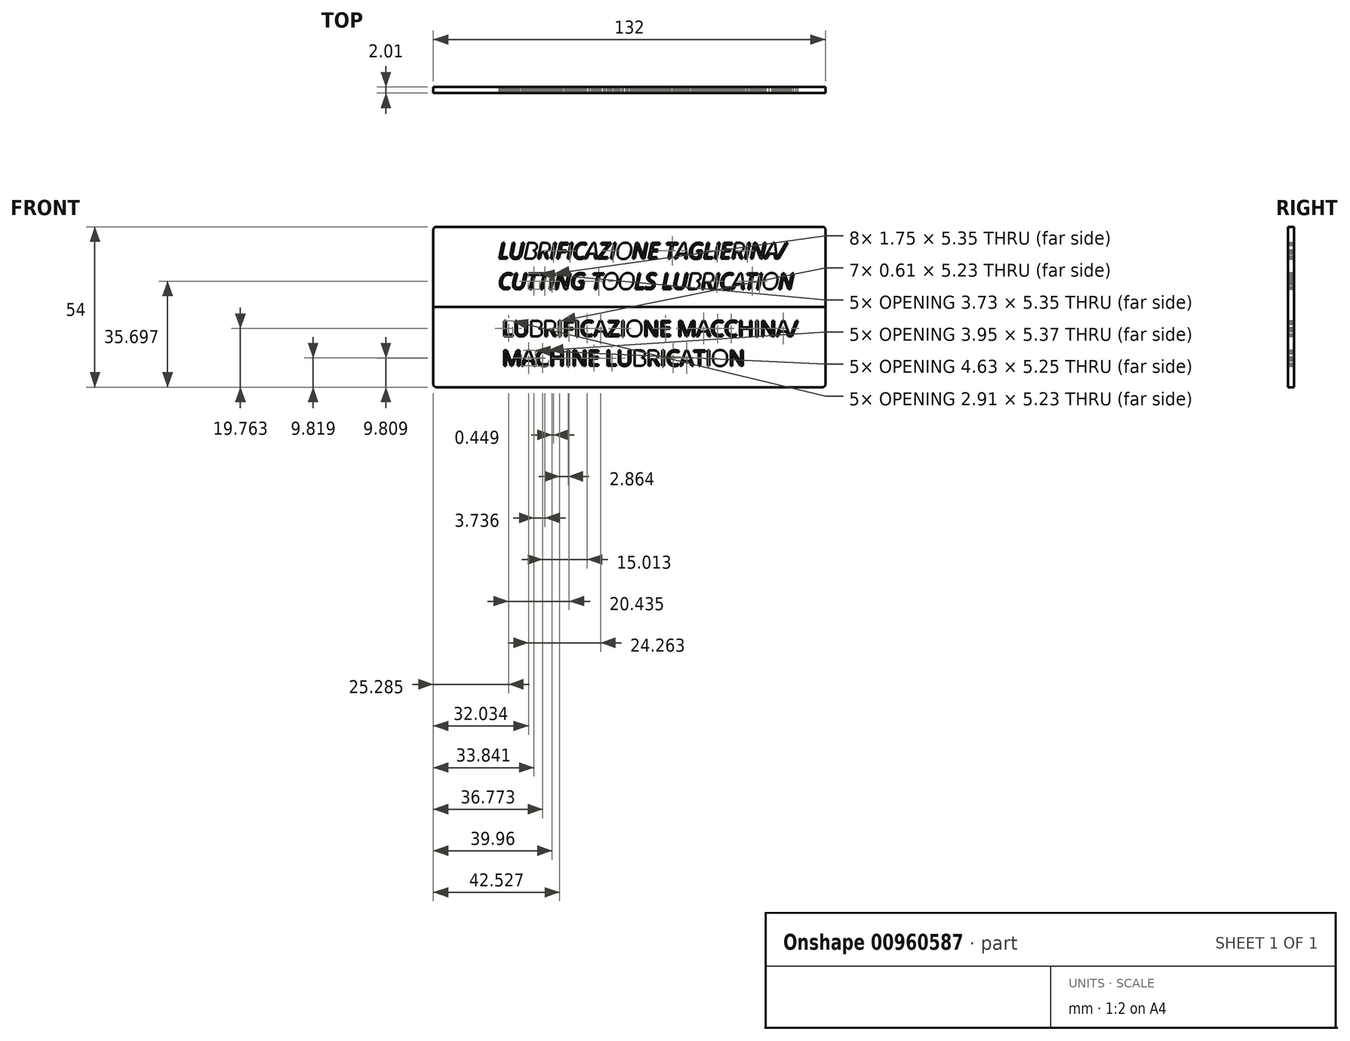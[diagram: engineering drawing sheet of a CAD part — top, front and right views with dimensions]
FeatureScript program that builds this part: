
annotation { "Feature Type Name" : "Feature", "Feature Type Description" : "" }
export const myFeature = defineFeature(function(context is Context, id is Id, definition is map)
    precondition{}
    {
        {
            var Q0;
            Q0=qCreatedBy(makeId("Front.planeOp"),FACE);
            var sketch = newSketch(context, id + "F0", { "sketchPlane" : qUnion([Q0])});
            skLineSegment(sketch, "E0.bottom", {"start": v(65, -27) * mm, "end": v(-65, -27) * mm});
            skLineSegment(sketch, "E0.top", {"start": v(65, 27) * mm, "end": v(-65, 27) * mm});
            skLineSegment(sketch, "E0.left", {"start": v(66, -26) * mm, "end": v(66, 26) * mm});
            skLineSegment(sketch, "E0.right", {"start": v(-66, -26) * mm, "end": v(-66, 26) * mm});
            skPoint(sketch, "E0.middle", {"position": v(0, 0) * mm});
            skLineSegment(sketch, "E1", {"start": v(-66, 0) * mm, "end": v(66, 0) * mm});
            skPoint(sketch, "E2.visualSharp", {"position": v(-66, 27) * mm});
            skArc(sketch, "E2.filletArc", {"start": v(-65, 27) * mm, "mid": v(-65.7, 26.7) * mm, "end": v(-66, 26) * mm});
            skPoint(sketch, "E3.visualSharp", {"position": v(66, 27) * mm});
            skArc(sketch, "E3.filletArc", {"start": v(66, 26) * mm, "mid": v(65.7, 26.7) * mm, "end": v(65, 27) * mm});
            skPoint(sketch, "E4.visualSharp", {"position": v(66, -27) * mm});
            skArc(sketch, "E4.filletArc", {"start": v(65, -27) * mm, "mid": v(65.7, -26.7) * mm, "end": v(66, -26) * mm});
            skPoint(sketch, "E5.visualSharp", {"position": v(-66, -27) * mm});
            skArc(sketch, "E5.filletArc", {"start": v(-66, -26) * mm, "mid": v(-65.7, -26.7) * mm, "end": v(-65, -27) * mm});
            skText(sketch, "E6", { "text": "LUBRIFICAZIONE TAGLIERINA/\nCUTTING TOOLS LUBRICATION", "fontName": "OpenSans-Italic.ttf"});
            skText(sketch, "E7", { "text": "LUBRIFICAZIONE MACCHINA/ \nMACHINE LUBRICATION", "fontName": "OpenSans-Regular.ttf"});
            const initialGuessF0  = {"E6": [-0.04416, 0.01622, 1, 0, 0.0054], "E7": [-0.04289, -0.00985, 1, 0, 0.00527]};
            skSetInitialGuess(sketch, initialGuessF0);
            skSolve(sketch);
        }
        {
            var Q0;
            Q0 = qSketchRegion(id + "F0", true);
            extrude(context, id + "F1", {"entities" : qUnion([Q0]), "depth" : 2 * mm, "offsetDistance" : 25 * mm});
        }
        {
            var Q0;
            Q0=makeQuery(id+"F1.opExtrude","CAP_FACE",FACE,{"disambiguationData":[OSD([sQuery(id+"F0.wireOp",EDGE,"E0.bottom"),sQuery(id+"F0.wireOp",EDGE,"E0.top"),sQuery(id+"F0.wireOp",EDGE,"E0.left"),sQuery(id+"F0.wireOp",EDGE,"E0.right"),sQuery(id+"F0.wireOp",EDGE,"E2.filletArc"),sQuery(id+"F0.wireOp",EDGE,"E3.filletArc"),sQuery(id+"F0.wireOp",EDGE,"E4.filletArc"),sQuery(id+"F0.wireOp",EDGE,"E5.filletArc"),sQuery(id+"F0.wireOp",EDGE,"E6.sketch_text.stroke-0"),sQuery(id+"F0.wireOp",EDGE,"E6.sketch_text.stroke-1"),sQuery(id+"F0.wireOp",EDGE,"E6.sketch_text.stroke-2"),sQuery(id+"F0.wireOp",EDGE,"E6.sketch_text.stroke-3"),sQuery(id+"F0.wireOp",EDGE,"E6.sketch_text.stroke-4"),sQuery(id+"F0.wireOp",EDGE,"E6.sketch_text.stroke-5"),sQuery(id+"F0.wireOp",EDGE,"E6.sketch_text.stroke-6"),sQuery(id+"F0.wireOp",EDGE,"E6.sketch_text.stroke-7"),sQuery(id+"F0.wireOp",EDGE,"E6.sketch_text.stroke-8"),sQuery(id+"F0.wireOp",EDGE,"E6.sketch_text.stroke-9"),sQuery(id+"F0.wireOp",EDGE,"E6.sketch_text.stroke-10"),sQuery(id+"F0.wireOp",EDGE,"E6.sketch_text.stroke-11"),sQuery(id+"F0.wireOp",EDGE,"E6.sketch_text.stroke-12"),sQuery(id+"F0.wireOp",EDGE,"E6.sketch_text.stroke-13"),sQuery(id+"F0.wireOp",EDGE,"E6.sketch_text.stroke-14"),sQuery(id+"F0.wireOp",EDGE,"E6.sketch_text.stroke-15"),sQuery(id+"F0.wireOp",EDGE,"E6.sketch_text.stroke-16"),sQuery(id+"F0.wireOp",EDGE,"E6.sketch_text.stroke-17"),sQuery(id+"F0.wireOp",EDGE,"E6.sketch_text.stroke-18"),sQuery(id+"F0.wireOp",EDGE,"E6.sketch_text.stroke-19"),sQuery(id+"F0.wireOp",EDGE,"E6.sketch_text.stroke-20"),sQuery(id+"F0.wireOp",EDGE,"E6.sketch_text.stroke-21"),sQuery(id+"F0.wireOp",EDGE,"E6.sketch_text.stroke-22"),sQuery(id+"F0.wireOp",EDGE,"E6.sketch_text.stroke-23"),sQuery(id+"F0.wireOp",EDGE,"E6.sketch_text.stroke-24"),sQuery(id+"F0.wireOp",EDGE,"E6.sketch_text.stroke-25"),sQuery(id+"F0.wireOp",EDGE,"E6.sketch_text.stroke-26"),sQuery(id+"F0.wireOp",EDGE,"E6.sketch_text.stroke-27"),sQuery(id+"F0.wireOp",EDGE,"E6.sketch_text.stroke-28"),sQuery(id+"F0.wireOp",EDGE,"E6.sketch_text.stroke-29"),sQuery(id+"F0.wireOp",EDGE,"E6.sketch_text.stroke-30"),sQuery(id+"F0.wireOp",EDGE,"E6.sketch_text.stroke-31"),sQuery(id+"F0.wireOp",EDGE,"E6.sketch_text.stroke-32"),sQuery(id+"F0.wireOp",EDGE,"E6.sketch_text.stroke-47"),sQuery(id+"F0.wireOp",EDGE,"E6.sketch_text.stroke-48"),sQuery(id+"F0.wireOp",EDGE,"E6.sketch_text.stroke-49"),sQuery(id+"F0.wireOp",EDGE,"E6.sketch_text.stroke-50"),sQuery(id+"F0.wireOp",EDGE,"E6.sketch_text.stroke-51"),sQuery(id+"F0.wireOp",EDGE,"E6.sketch_text.stroke-52"),sQuery(id+"F0.wireOp",EDGE,"E6.sketch_text.stroke-53"),sQuery(id+"F0.wireOp",EDGE,"E6.sketch_text.stroke-54"),sQuery(id+"F0.wireOp",EDGE,"E6.sketch_text.stroke-55"),sQuery(id+"F0.wireOp",EDGE,"E6.sketch_text.stroke-56"),sQuery(id+"F0.wireOp",EDGE,"E6.sketch_text.stroke-64"),sQuery(id+"F0.wireOp",EDGE,"E6.sketch_text.stroke-65"),sQuery(id+"F0.wireOp",EDGE,"E6.sketch_text.stroke-66"),sQuery(id+"F0.wireOp",EDGE,"E6.sketch_text.stroke-67"),sQuery(id+"F0.wireOp",EDGE,"E6.sketch_text.stroke-68"),sQuery(id+"F0.wireOp",EDGE,"E6.sketch_text.stroke-69"),sQuery(id+"F0.wireOp",EDGE,"E6.sketch_text.stroke-70"),sQuery(id+"F0.wireOp",EDGE,"E6.sketch_text.stroke-71"),sQuery(id+"F0.wireOp",EDGE,"E6.sketch_text.stroke-72"),sQuery(id+"F0.wireOp",EDGE,"E6.sketch_text.stroke-73"),sQuery(id+"F0.wireOp",EDGE,"E6.sketch_text.stroke-74"),sQuery(id+"F0.wireOp",EDGE,"E6.sketch_text.stroke-75"),sQuery(id+"F0.wireOp",EDGE,"E6.sketch_text.stroke-76"),sQuery(id+"F0.wireOp",EDGE,"E6.sketch_text.stroke-77"),sQuery(id+"F0.wireOp",EDGE,"E6.sketch_text.stroke-78"),sQuery(id+"F0.wireOp",EDGE,"E6.sketch_text.stroke-79"),sQuery(id+"F0.wireOp",EDGE,"E6.sketch_text.stroke-80"),sQuery(id+"F0.wireOp",EDGE,"E6.sketch_text.stroke-81"),sQuery(id+"F0.wireOp",EDGE,"E6.sketch_text.stroke-82"),sQuery(id+"F0.wireOp",EDGE,"E6.sketch_text.stroke-83"),sQuery(id+"F0.wireOp",EDGE,"E6.sketch_text.stroke-84"),sQuery(id+"F0.wireOp",EDGE,"E6.sketch_text.stroke-85"),sQuery(id+"F0.wireOp",EDGE,"E6.sketch_text.stroke-86"),sQuery(id+"F0.wireOp",EDGE,"E6.sketch_text.stroke-87"),sQuery(id+"F0.wireOp",EDGE,"E6.sketch_text.stroke-88"),sQuery(id+"F0.wireOp",EDGE,"E6.sketch_text.stroke-89"),sQuery(id+"F0.wireOp",EDGE,"E6.sketch_text.stroke-90"),sQuery(id+"F0.wireOp",EDGE,"E6.sketch_text.stroke-91"),sQuery(id+"F0.wireOp",EDGE,"E6.sketch_text.stroke-92"),sQuery(id+"F0.wireOp",EDGE,"E6.sketch_text.stroke-93"),sQuery(id+"F0.wireOp",EDGE,"E6.sketch_text.stroke-94"),sQuery(id+"F0.wireOp",EDGE,"E6.sketch_text.stroke-95"),sQuery(id+"F0.wireOp",EDGE,"E6.sketch_text.stroke-96"),sQuery(id+"F0.wireOp",EDGE,"E6.sketch_text.stroke-97"),sQuery(id+"F0.wireOp",EDGE,"E6.sketch_text.stroke-98"),sQuery(id+"F0.wireOp",EDGE,"E6.sketch_text.stroke-99"),sQuery(id+"F0.wireOp",EDGE,"E6.sketch_text.stroke-100"),sQuery(id+"F0.wireOp",EDGE,"E6.sketch_text.stroke-101"),sQuery(id+"F0.wireOp",EDGE,"E6.sketch_text.stroke-102"),sQuery(id+"F0.wireOp",EDGE,"E6.sketch_text.stroke-103"),sQuery(id+"F0.wireOp",EDGE,"E6.sketch_text.stroke-104"),sQuery(id+"F0.wireOp",EDGE,"E6.sketch_text.stroke-105"),sQuery(id+"F0.wireOp",EDGE,"E6.sketch_text.stroke-106"),sQuery(id+"F0.wireOp",EDGE,"E6.sketch_text.stroke-112"),sQuery(id+"F0.wireOp",EDGE,"E6.sketch_text.stroke-113"),sQuery(id+"F0.wireOp",EDGE,"E6.sketch_text.stroke-114"),sQuery(id+"F0.wireOp",EDGE,"E6.sketch_text.stroke-115"),sQuery(id+"F0.wireOp",EDGE,"E6.sketch_text.stroke-116"),sQuery(id+"F0.wireOp",EDGE,"E6.sketch_text.stroke-117"),sQuery(id+"F0.wireOp",EDGE,"E6.sketch_text.stroke-118"),sQuery(id+"F0.wireOp",EDGE,"E6.sketch_text.stroke-119"),sQuery(id+"F0.wireOp",EDGE,"E6.sketch_text.stroke-120"),sQuery(id+"F0.wireOp",EDGE,"E6.sketch_text.stroke-121"),sQuery(id+"F0.wireOp",EDGE,"E6.sketch_text.stroke-122"),sQuery(id+"F0.wireOp",EDGE,"E6.sketch_text.stroke-123"),sQuery(id+"F0.wireOp",EDGE,"E6.sketch_text.stroke-124"),sQuery(id+"F0.wireOp",EDGE,"E6.sketch_text.stroke-125"),sQuery(id+"F0.wireOp",EDGE,"E6.sketch_text.stroke-126"),sQuery(id+"F0.wireOp",EDGE,"E6.sketch_text.stroke-127"),sQuery(id+"F0.wireOp",EDGE,"E6.sketch_text.stroke-128"),sQuery(id+"F0.wireOp",EDGE,"E6.sketch_text.stroke-129"),sQuery(id+"F0.wireOp",EDGE,"E6.sketch_text.stroke-130"),sQuery(id+"F0.wireOp",EDGE,"E6.sketch_text.stroke-131"),sQuery(id+"F0.wireOp",EDGE,"E6.sketch_text.stroke-132"),sQuery(id+"F0.wireOp",EDGE,"E6.sketch_text.stroke-133"),sQuery(id+"F0.wireOp",EDGE,"E6.sketch_text.stroke-134"),sQuery(id+"F0.wireOp",EDGE,"E6.sketch_text.stroke-135"),sQuery(id+"F0.wireOp",EDGE,"E6.sketch_text.stroke-146"),sQuery(id+"F0.wireOp",EDGE,"E6.sketch_text.stroke-147"),sQuery(id+"F0.wireOp",EDGE,"E6.sketch_text.stroke-148"),sQuery(id+"F0.wireOp",EDGE,"E6.sketch_text.stroke-149"),sQuery(id+"F0.wireOp",EDGE,"E6.sketch_text.stroke-150"),sQuery(id+"F0.wireOp",EDGE,"E6.sketch_text.stroke-151"),sQuery(id+"F0.wireOp",EDGE,"E6.sketch_text.stroke-152"),sQuery(id+"F0.wireOp",EDGE,"E6.sketch_text.stroke-153"),sQuery(id+"F0.wireOp",EDGE,"E6.sketch_text.stroke-154"),sQuery(id+"F0.wireOp",EDGE,"E6.sketch_text.stroke-155"),sQuery(id+"F0.wireOp",EDGE,"E6.sketch_text.stroke-156"),sQuery(id+"F0.wireOp",EDGE,"E6.sketch_text.stroke-157"),sQuery(id+"F0.wireOp",EDGE,"E6.sketch_text.stroke-158"),sQuery(id+"F0.wireOp",EDGE,"E6.sketch_text.stroke-159"),sQuery(id+"F0.wireOp",EDGE,"E6.sketch_text.stroke-160"),sQuery(id+"F0.wireOp",EDGE,"E6.sketch_text.stroke-161"),sQuery(id+"F0.wireOp",EDGE,"E6.sketch_text.stroke-162"),sQuery(id+"F0.wireOp",EDGE,"E6.sketch_text.stroke-163"),sQuery(id+"F0.wireOp",EDGE,"E6.sketch_text.stroke-164"),sQuery(id+"F0.wireOp",EDGE,"E6.sketch_text.stroke-165"),sQuery(id+"F0.wireOp",EDGE,"E6.sketch_text.stroke-166"),sQuery(id+"F0.wireOp",EDGE,"E6.sketch_text.stroke-167"),sQuery(id+"F0.wireOp",EDGE,"E6.sketch_text.stroke-168"),sQuery(id+"F0.wireOp",EDGE,"E6.sketch_text.stroke-169"),sQuery(id+"F0.wireOp",EDGE,"E6.sketch_text.stroke-170"),sQuery(id+"F0.wireOp",EDGE,"E6.sketch_text.stroke-171"),sQuery(id+"F0.wireOp",EDGE,"E6.sketch_text.stroke-172"),sQuery(id+"F0.wireOp",EDGE,"E6.sketch_text.stroke-173"),sQuery(id+"F0.wireOp",EDGE,"E6.sketch_text.stroke-174"),sQuery(id+"F0.wireOp",EDGE,"E6.sketch_text.stroke-175"),sQuery(id+"F0.wireOp",EDGE,"E6.sketch_text.stroke-176"),sQuery(id+"F0.wireOp",EDGE,"E6.sketch_text.stroke-177"),sQuery(id+"F0.wireOp",EDGE,"E6.sketch_text.stroke-178"),sQuery(id+"F0.wireOp",EDGE,"E6.sketch_text.stroke-179"),sQuery(id+"F0.wireOp",EDGE,"E6.sketch_text.stroke-180"),sQuery(id+"F0.wireOp",EDGE,"E6.sketch_text.stroke-181"),sQuery(id+"F0.wireOp",EDGE,"E6.sketch_text.stroke-182"),sQuery(id+"F0.wireOp",EDGE,"E6.sketch_text.stroke-183"),sQuery(id+"F0.wireOp",EDGE,"E6.sketch_text.stroke-184"),sQuery(id+"F0.wireOp",EDGE,"E6.sketch_text.stroke-185"),sQuery(id+"F0.wireOp",EDGE,"E6.sketch_text.stroke-186"),sQuery(id+"F0.wireOp",EDGE,"E6.sketch_text.stroke-187"),sQuery(id+"F0.wireOp",EDGE,"E6.sketch_text.stroke-193"),sQuery(id+"F0.wireOp",EDGE,"E6.sketch_text.stroke-194"),sQuery(id+"F0.wireOp",EDGE,"E6.sketch_text.stroke-195"),sQuery(id+"F0.wireOp",EDGE,"E6.sketch_text.stroke-196"),sQuery(id+"F0.wireOp",EDGE,"E6.sketch_text.stroke-197"),sQuery(id+"F0.wireOp",EDGE,"E6.sketch_text.stroke-198"),sQuery(id+"F0.wireOp",EDGE,"E6.sketch_text.stroke-199"),sQuery(id+"F0.wireOp",EDGE,"E6.sketch_text.stroke-200"),sQuery(id+"F0.wireOp",EDGE,"E6.sketch_text.stroke-201"),sQuery(id+"F0.wireOp",EDGE,"E6.sketch_text.stroke-202"),sQuery(id+"F0.wireOp",EDGE,"E6.sketch_text.stroke-203"),sQuery(id+"F0.wireOp",EDGE,"E6.sketch_text.stroke-204"),sQuery(id+"F0.wireOp",EDGE,"E6.sketch_text.stroke-205"),sQuery(id+"F0.wireOp",EDGE,"E6.sketch_text.stroke-206"),sQuery(id+"F0.wireOp",EDGE,"E6.sketch_text.stroke-207"),sQuery(id+"F0.wireOp",EDGE,"E6.sketch_text.stroke-208"),sQuery(id+"F0.wireOp",EDGE,"E6.sketch_text.stroke-209"),sQuery(id+"F0.wireOp",EDGE,"E6.sketch_text.stroke-210"),sQuery(id+"F0.wireOp",EDGE,"E6.sketch_text.stroke-211"),sQuery(id+"F0.wireOp",EDGE,"E6.sketch_text.stroke-212"),sQuery(id+"F0.wireOp",EDGE,"E6.sketch_text.stroke-213"),sQuery(id+"F0.wireOp",EDGE,"E6.sketch_text.stroke-214"),sQuery(id+"F0.wireOp",EDGE,"E6.sketch_text.stroke-215"),sQuery(id+"F0.wireOp",EDGE,"E6.sketch_text.stroke-216"),sQuery(id+"F0.wireOp",EDGE,"E6.sketch_text.stroke-217"),sQuery(id+"F0.wireOp",EDGE,"E6.sketch_text.stroke-218"),sQuery(id+"F0.wireOp",EDGE,"E6.sketch_text.stroke-219"),sQuery(id+"F0.wireOp",EDGE,"E6.sketch_text.stroke-220"),sQuery(id+"F0.wireOp",EDGE,"E6.sketch_text.stroke-221"),sQuery(id+"F0.wireOp",EDGE,"E6.sketch_text.stroke-222"),sQuery(id+"F0.wireOp",EDGE,"E6.sketch_text.stroke-223"),sQuery(id+"F0.wireOp",EDGE,"E6.sketch_text.stroke-224"),sQuery(id+"F0.wireOp",EDGE,"E6.sketch_text.stroke-225"),sQuery(id+"F0.wireOp",EDGE,"E6.sketch_text.stroke-226"),sQuery(id+"F0.wireOp",EDGE,"E6.sketch_text.stroke-227"),sQuery(id+"F0.wireOp",EDGE,"E6.sketch_text.stroke-228"),sQuery(id+"F0.wireOp",EDGE,"E6.sketch_text.stroke-229"),sQuery(id+"F0.wireOp",EDGE,"E6.sketch_text.stroke-230"),sQuery(id+"F0.wireOp",EDGE,"E6.sketch_text.stroke-231"),sQuery(id+"F0.wireOp",EDGE,"E6.sketch_text.stroke-232"),sQuery(id+"F0.wireOp",EDGE,"E6.sketch_text.stroke-233"),sQuery(id+"F0.wireOp",EDGE,"E6.sketch_text.stroke-234"),sQuery(id+"F0.wireOp",EDGE,"E6.sketch_text.stroke-235"),sQuery(id+"F0.wireOp",EDGE,"E6.sketch_text.stroke-236"),sQuery(id+"F0.wireOp",EDGE,"E6.sketch_text.stroke-237"),sQuery(id+"F0.wireOp",EDGE,"E6.sketch_text.stroke-238"),sQuery(id+"F0.wireOp",EDGE,"E6.sketch_text.stroke-239"),sQuery(id+"F0.wireOp",EDGE,"E6.sketch_text.stroke-240"),sQuery(id+"F0.wireOp",EDGE,"E6.sketch_text.stroke-241"),sQuery(id+"F0.wireOp",EDGE,"E6.sketch_text.stroke-242"),sQuery(id+"F0.wireOp",EDGE,"E6.sketch_text.stroke-243"),sQuery(id+"F0.wireOp",EDGE,"E6.sketch_text.stroke-244"),sQuery(id+"F0.wireOp",EDGE,"E6.sketch_text.stroke-245"),sQuery(id+"F0.wireOp",EDGE,"E6.sketch_text.stroke-246"),sQuery(id+"F0.wireOp",EDGE,"E6.sketch_text.stroke-254"),sQuery(id+"F0.wireOp",EDGE,"E6.sketch_text.stroke-255"),sQuery(id+"F0.wireOp",EDGE,"E6.sketch_text.stroke-256"),sQuery(id+"F0.wireOp",EDGE,"E6.sketch_text.stroke-257"),sQuery(id+"F0.wireOp",EDGE,"E6.sketch_text.stroke-258"),sQuery(id+"F0.wireOp",EDGE,"E6.sketch_text.stroke-259"),sQuery(id+"F0.wireOp",EDGE,"E6.sketch_text.stroke-260"),sQuery(id+"F0.wireOp",EDGE,"E6.sketch_text.stroke-261"),sQuery(id+"F0.wireOp",EDGE,"E6.sketch_text.stroke-262"),sQuery(id+"F0.wireOp",EDGE,"E6.sketch_text.stroke-263"),sQuery(id+"F0.wireOp",EDGE,"E6.sketch_text.stroke-264"),sQuery(id+"F0.wireOp",EDGE,"E6.sketch_text.stroke-265"),sQuery(id+"F0.wireOp",EDGE,"E6.sketch_text.stroke-266"),sQuery(id+"F0.wireOp",EDGE,"E6.sketch_text.stroke-267"),sQuery(id+"F0.wireOp",EDGE,"E6.sketch_text.stroke-268"),sQuery(id+"F0.wireOp",EDGE,"E6.sketch_text.stroke-269"),sQuery(id+"F0.wireOp",EDGE,"E6.sketch_text.stroke-270"),sQuery(id+"F0.wireOp",EDGE,"E6.sketch_text.stroke-271"),sQuery(id+"F0.wireOp",EDGE,"E6.sketch_text.stroke-272"),sQuery(id+"F0.wireOp",EDGE,"E6.sketch_text.stroke-273"),sQuery(id+"F0.wireOp",EDGE,"E6.sketch_text.stroke-274"),sQuery(id+"F0.wireOp",EDGE,"E6.sketch_text.stroke-275"),sQuery(id+"F0.wireOp",EDGE,"E6.sketch_text.stroke-276"),sQuery(id+"F0.wireOp",EDGE,"E6.sketch_text.stroke-277"),sQuery(id+"F0.wireOp",EDGE,"E6.sketch_text.stroke-278"),sQuery(id+"F0.wireOp",EDGE,"E6.sketch_text.stroke-279"),sQuery(id+"F0.wireOp",EDGE,"E6.sketch_text.stroke-285"),sQuery(id+"F0.wireOp",EDGE,"E6.sketch_text.stroke-286"),sQuery(id+"F0.wireOp",EDGE,"E6.sketch_text.stroke-287"),sQuery(id+"F0.wireOp",EDGE,"E6.sketch_text.stroke-288"),sQuery(id+"F0.wireOp",EDGE,"E6.sketch_text.stroke-289"),sQuery(id+"F0.wireOp",EDGE,"E6.sketch_text.stroke-290"),sQuery(id+"F0.wireOp",EDGE,"E6.sketch_text.stroke-291"),sQuery(id+"F0.wireOp",EDGE,"E6.sketch_text.stroke-292"),sQuery(id+"F0.wireOp",EDGE,"E6.sketch_text.stroke-293"),sQuery(id+"F0.wireOp",EDGE,"E6.sketch_text.stroke-294"),sQuery(id+"F0.wireOp",EDGE,"E6.sketch_text.stroke-295"),sQuery(id+"F0.wireOp",EDGE,"E6.sketch_text.stroke-296"),sQuery(id+"F0.wireOp",EDGE,"E6.sketch_text.stroke-297"),sQuery(id+"F0.wireOp",EDGE,"E6.sketch_text.stroke-298"),sQuery(id+"F0.wireOp",EDGE,"E6.sketch_text.stroke-299"),sQuery(id+"F0.wireOp",EDGE,"E6.sketch_text.stroke-300"),sQuery(id+"F0.wireOp",EDGE,"E6.sketch_text.stroke-301"),sQuery(id+"F0.wireOp",EDGE,"E6.sketch_text.stroke-302"),sQuery(id+"F0.wireOp",EDGE,"E6.sketch_text.stroke-303"),sQuery(id+"F0.wireOp",EDGE,"E6.sketch_text.stroke-304"),sQuery(id+"F0.wireOp",EDGE,"E6.sketch_text.stroke-305"),sQuery(id+"F0.wireOp",EDGE,"E6.sketch_text.stroke-306"),sQuery(id+"F0.wireOp",EDGE,"E6.sketch_text.stroke-307"),sQuery(id+"F0.wireOp",EDGE,"E6.sketch_text.stroke-308"),sQuery(id+"F0.wireOp",EDGE,"E6.sketch_text.stroke-309"),sQuery(id+"F0.wireOp",EDGE,"E6.sketch_text.stroke-310"),sQuery(id+"F0.wireOp",EDGE,"E6.sketch_text.stroke-311"),sQuery(id+"F0.wireOp",EDGE,"E6.sketch_text.stroke-312"),sQuery(id+"F0.wireOp",EDGE,"E6.sketch_text.stroke-313"),sQuery(id+"F0.wireOp",EDGE,"E6.sketch_text.stroke-314"),sQuery(id+"F0.wireOp",EDGE,"E6.sketch_text.stroke-315"),sQuery(id+"F0.wireOp",EDGE,"E6.sketch_text.stroke-316"),sQuery(id+"F0.wireOp",EDGE,"E6.sketch_text.stroke-317"),sQuery(id+"F0.wireOp",EDGE,"E6.sketch_text.stroke-318"),sQuery(id+"F0.wireOp",EDGE,"E6.sketch_text.stroke-319"),sQuery(id+"F0.wireOp",EDGE,"E6.sketch_text.stroke-320"),sQuery(id+"F0.wireOp",EDGE,"E6.sketch_text.stroke-321"),sQuery(id+"F0.wireOp",EDGE,"E6.sketch_text.stroke-322"),sQuery(id+"F0.wireOp",EDGE,"E6.sketch_text.stroke-323"),sQuery(id+"F0.wireOp",EDGE,"E6.sketch_text.stroke-324"),sQuery(id+"F0.wireOp",EDGE,"E6.sketch_text.stroke-325"),sQuery(id+"F0.wireOp",EDGE,"E6.sketch_text.stroke-326"),sQuery(id+"F0.wireOp",EDGE,"E6.sketch_text.stroke-327"),sQuery(id+"F0.wireOp",EDGE,"E6.sketch_text.stroke-328"),sQuery(id+"F0.wireOp",EDGE,"E6.sketch_text.stroke-329"),sQuery(id+"F0.wireOp",EDGE,"E6.sketch_text.stroke-330"),sQuery(id+"F0.wireOp",EDGE,"E6.sketch_text.stroke-331"),sQuery(id+"F0.wireOp",EDGE,"E6.sketch_text.stroke-332"),sQuery(id+"F0.wireOp",EDGE,"E6.sketch_text.stroke-333"),sQuery(id+"F0.wireOp",EDGE,"E6.sketch_text.stroke-334"),sQuery(id+"F0.wireOp",EDGE,"E6.sketch_text.stroke-335"),sQuery(id+"F0.wireOp",EDGE,"E6.sketch_text.stroke-336"),sQuery(id+"F0.wireOp",EDGE,"E6.sketch_text.stroke-337"),sQuery(id+"F0.wireOp",EDGE,"E6.sketch_text.stroke-338"),sQuery(id+"F0.wireOp",EDGE,"E6.sketch_text.stroke-339"),sQuery(id+"F0.wireOp",EDGE,"E6.sketch_text.stroke-340"),sQuery(id+"F0.wireOp",EDGE,"E6.sketch_text.stroke-341"),sQuery(id+"F0.wireOp",EDGE,"E6.sketch_text.stroke-342"),sQuery(id+"F0.wireOp",EDGE,"E6.sketch_text.stroke-343"),sQuery(id+"F0.wireOp",EDGE,"E6.sketch_text.stroke-344"),sQuery(id+"F0.wireOp",EDGE,"E6.sketch_text.stroke-345"),sQuery(id+"F0.wireOp",EDGE,"E6.sketch_text.stroke-346"),sQuery(id+"F0.wireOp",EDGE,"E6.sketch_text.stroke-347"),sQuery(id+"F0.wireOp",EDGE,"E6.sketch_text.stroke-348"),sQuery(id+"F0.wireOp",EDGE,"E6.sketch_text.stroke-349"),sQuery(id+"F0.wireOp",EDGE,"E6.sketch_text.stroke-350"),sQuery(id+"F0.wireOp",EDGE,"E6.sketch_text.stroke-351"),sQuery(id+"F0.wireOp",EDGE,"E6.sketch_text.stroke-352"),sQuery(id+"F0.wireOp",EDGE,"E6.sketch_text.stroke-353"),sQuery(id+"F0.wireOp",EDGE,"E6.sketch_text.stroke-354"),sQuery(id+"F0.wireOp",EDGE,"E6.sketch_text.stroke-355"),sQuery(id+"F0.wireOp",EDGE,"E6.sketch_text.stroke-356"),sQuery(id+"F0.wireOp",EDGE,"E6.sketch_text.stroke-357"),sQuery(id+"F0.wireOp",EDGE,"E6.sketch_text.stroke-358"),sQuery(id+"F0.wireOp",EDGE,"E6.sketch_text.stroke-359"),sQuery(id+"F0.wireOp",EDGE,"E6.sketch_text.stroke-360"),sQuery(id+"F0.wireOp",EDGE,"E6.sketch_text.stroke-361"),sQuery(id+"F0.wireOp",EDGE,"E6.sketch_text.stroke-362"),sQuery(id+"F0.wireOp",EDGE,"E6.sketch_text.stroke-363"),sQuery(id+"F0.wireOp",EDGE,"E6.sketch_text.stroke-364"),sQuery(id+"F0.wireOp",EDGE,"E6.sketch_text.stroke-365"),sQuery(id+"F0.wireOp",EDGE,"E6.sketch_text.stroke-366"),sQuery(id+"F0.wireOp",EDGE,"E6.sketch_text.stroke-367"),sQuery(id+"F0.wireOp",EDGE,"E6.sketch_text.stroke-368"),sQuery(id+"F0.wireOp",EDGE,"E6.sketch_text.stroke-369"),sQuery(id+"F0.wireOp",EDGE,"E6.sketch_text.stroke-370"),sQuery(id+"F0.wireOp",EDGE,"E6.sketch_text.stroke-371"),sQuery(id+"F0.wireOp",EDGE,"E6.sketch_text.stroke-372"),sQuery(id+"F0.wireOp",EDGE,"E6.sketch_text.stroke-373"),sQuery(id+"F0.wireOp",EDGE,"E6.sketch_text.stroke-374"),sQuery(id+"F0.wireOp",EDGE,"E6.sketch_text.stroke-375"),sQuery(id+"F0.wireOp",EDGE,"E6.sketch_text.stroke-376"),sQuery(id+"F0.wireOp",EDGE,"E6.sketch_text.stroke-377"),sQuery(id+"F0.wireOp",EDGE,"E6.sketch_text.stroke-378"),sQuery(id+"F0.wireOp",EDGE,"E6.sketch_text.stroke-379"),sQuery(id+"F0.wireOp",EDGE,"E6.sketch_text.stroke-380"),sQuery(id+"F0.wireOp",EDGE,"E6.sketch_text.stroke-381"),sQuery(id+"F0.wireOp",EDGE,"E6.sketch_text.stroke-382"),sQuery(id+"F0.wireOp",EDGE,"E6.sketch_text.stroke-383"),sQuery(id+"F0.wireOp",EDGE,"E6.sketch_text.stroke-384"),sQuery(id+"F0.wireOp",EDGE,"E6.sketch_text.stroke-385"),sQuery(id+"F0.wireOp",EDGE,"E6.sketch_text.stroke-386"),sQuery(id+"F0.wireOp",EDGE,"E6.sketch_text.stroke-387"),sQuery(id+"F0.wireOp",EDGE,"E6.sketch_text.stroke-388"),sQuery(id+"F0.wireOp",EDGE,"E6.sketch_text.stroke-389"),sQuery(id+"F0.wireOp",EDGE,"E6.sketch_text.stroke-390"),sQuery(id+"F0.wireOp",EDGE,"E6.sketch_text.stroke-391"),sQuery(id+"F0.wireOp",EDGE,"E6.sketch_text.stroke-392"),sQuery(id+"F0.wireOp",EDGE,"E6.sketch_text.stroke-393"),sQuery(id+"F0.wireOp",EDGE,"E6.sketch_text.stroke-394"),sQuery(id+"F0.wireOp",EDGE,"E6.sketch_text.stroke-395"),sQuery(id+"F0.wireOp",EDGE,"E6.sketch_text.stroke-406"),sQuery(id+"F0.wireOp",EDGE,"E6.sketch_text.stroke-407"),sQuery(id+"F0.wireOp",EDGE,"E6.sketch_text.stroke-408"),sQuery(id+"F0.wireOp",EDGE,"E6.sketch_text.stroke-409"),sQuery(id+"F0.wireOp",EDGE,"E6.sketch_text.stroke-410"),sQuery(id+"F0.wireOp",EDGE,"E6.sketch_text.stroke-411"),sQuery(id+"F0.wireOp",EDGE,"E6.sketch_text.stroke-412"),sQuery(id+"F0.wireOp",EDGE,"E6.sketch_text.stroke-413"),sQuery(id+"F0.wireOp",EDGE,"E6.sketch_text.stroke-414"),sQuery(id+"F0.wireOp",EDGE,"E6.sketch_text.stroke-415"),sQuery(id+"F0.wireOp",EDGE,"E6.sketch_text.stroke-426"),sQuery(id+"F0.wireOp",EDGE,"E6.sketch_text.stroke-427"),sQuery(id+"F0.wireOp",EDGE,"E6.sketch_text.stroke-428"),sQuery(id+"F0.wireOp",EDGE,"E6.sketch_text.stroke-429"),sQuery(id+"F0.wireOp",EDGE,"E6.sketch_text.stroke-430"),sQuery(id+"F0.wireOp",EDGE,"E6.sketch_text.stroke-431"),sQuery(id+"F0.wireOp",EDGE,"E6.sketch_text.stroke-432"),sQuery(id+"F0.wireOp",EDGE,"E6.sketch_text.stroke-433"),sQuery(id+"F0.wireOp",EDGE,"E6.sketch_text.stroke-434"),sQuery(id+"F0.wireOp",EDGE,"E6.sketch_text.stroke-435"),sQuery(id+"F0.wireOp",EDGE,"E6.sketch_text.stroke-436"),sQuery(id+"F0.wireOp",EDGE,"E6.sketch_text.stroke-437"),sQuery(id+"F0.wireOp",EDGE,"E6.sketch_text.stroke-438"),sQuery(id+"F0.wireOp",EDGE,"E6.sketch_text.stroke-439"),sQuery(id+"F0.wireOp",EDGE,"E6.sketch_text.stroke-440"),sQuery(id+"F0.wireOp",EDGE,"E6.sketch_text.stroke-441"),sQuery(id+"F0.wireOp",EDGE,"E6.sketch_text.stroke-442"),sQuery(id+"F0.wireOp",EDGE,"E6.sketch_text.stroke-443"),sQuery(id+"F0.wireOp",EDGE,"E6.sketch_text.stroke-444"),sQuery(id+"F0.wireOp",EDGE,"E6.sketch_text.stroke-445"),sQuery(id+"F0.wireOp",EDGE,"E6.sketch_text.stroke-446"),sQuery(id+"F0.wireOp",EDGE,"E6.sketch_text.stroke-447"),sQuery(id+"F0.wireOp",EDGE,"E6.sketch_text.stroke-448"),sQuery(id+"F0.wireOp",EDGE,"E6.sketch_text.stroke-449"),sQuery(id+"F0.wireOp",EDGE,"E6.sketch_text.stroke-450"),sQuery(id+"F0.wireOp",EDGE,"E6.sketch_text.stroke-451"),sQuery(id+"F0.wireOp",EDGE,"E6.sketch_text.stroke-452"),sQuery(id+"F0.wireOp",EDGE,"E6.sketch_text.stroke-453"),sQuery(id+"F0.wireOp",EDGE,"E6.sketch_text.stroke-454"),sQuery(id+"F0.wireOp",EDGE,"E6.sketch_text.stroke-455"),sQuery(id+"F0.wireOp",EDGE,"E6.sketch_text.stroke-456"),sQuery(id+"F0.wireOp",EDGE,"E6.sketch_text.stroke-457"),sQuery(id+"F0.wireOp",EDGE,"E6.sketch_text.stroke-458"),sQuery(id+"F0.wireOp",EDGE,"E6.sketch_text.stroke-459"),sQuery(id+"F0.wireOp",EDGE,"E6.sketch_text.stroke-460"),sQuery(id+"F0.wireOp",EDGE,"E6.sketch_text.stroke-461"),sQuery(id+"F0.wireOp",EDGE,"E6.sketch_text.stroke-462"),sQuery(id+"F0.wireOp",EDGE,"E6.sketch_text.stroke-463"),sQuery(id+"F0.wireOp",EDGE,"E6.sketch_text.stroke-464"),sQuery(id+"F0.wireOp",EDGE,"E6.sketch_text.stroke-465"),sQuery(id+"F0.wireOp",EDGE,"E6.sketch_text.stroke-466"),sQuery(id+"F0.wireOp",EDGE,"E6.sketch_text.stroke-467"),sQuery(id+"F0.wireOp",EDGE,"E6.sketch_text.stroke-468"),sQuery(id+"F0.wireOp",EDGE,"E6.sketch_text.stroke-469"),sQuery(id+"F0.wireOp",EDGE,"E6.sketch_text.stroke-470"),sQuery(id+"F0.wireOp",EDGE,"E6.sketch_text.stroke-471"),sQuery(id+"F0.wireOp",EDGE,"E6.sketch_text.stroke-472"),sQuery(id+"F0.wireOp",EDGE,"E6.sketch_text.stroke-473"),sQuery(id+"F0.wireOp",EDGE,"E6.sketch_text.stroke-474"),sQuery(id+"F0.wireOp",EDGE,"E6.sketch_text.stroke-475"),sQuery(id+"F0.wireOp",EDGE,"E6.sketch_text.stroke-476"),sQuery(id+"F0.wireOp",EDGE,"E6.sketch_text.stroke-477"),sQuery(id+"F0.wireOp",EDGE,"E6.sketch_text.stroke-478"),sQuery(id+"F0.wireOp",EDGE,"E6.sketch_text.stroke-479"),sQuery(id+"F0.wireOp",EDGE,"E6.sketch_text.stroke-480"),sQuery(id+"F0.wireOp",EDGE,"E6.sketch_text.stroke-481"),sQuery(id+"F0.wireOp",EDGE,"E6.sketch_text.stroke-482"),sQuery(id+"F0.wireOp",EDGE,"E6.sketch_text.stroke-483"),sQuery(id+"F0.wireOp",EDGE,"E6.sketch_text.stroke-484"),sQuery(id+"F0.wireOp",EDGE,"E6.sketch_text.stroke-485"),sQuery(id+"F0.wireOp",EDGE,"E6.sketch_text.stroke-486"),sQuery(id+"F0.wireOp",EDGE,"E6.sketch_text.stroke-487"),sQuery(id+"F0.wireOp",EDGE,"E6.sketch_text.stroke-488"),sQuery(id+"F0.wireOp",EDGE,"E6.sketch_text.stroke-489"),sQuery(id+"F0.wireOp",EDGE,"E6.sketch_text.stroke-490"),sQuery(id+"F0.wireOp",EDGE,"E6.sketch_text.stroke-491"),sQuery(id+"F0.wireOp",EDGE,"E6.sketch_text.stroke-506"),sQuery(id+"F0.wireOp",EDGE,"E6.sketch_text.stroke-507"),sQuery(id+"F0.wireOp",EDGE,"E6.sketch_text.stroke-508"),sQuery(id+"F0.wireOp",EDGE,"E6.sketch_text.stroke-509"),sQuery(id+"F0.wireOp",EDGE,"E6.sketch_text.stroke-510"),sQuery(id+"F0.wireOp",EDGE,"E6.sketch_text.stroke-511"),sQuery(id+"F0.wireOp",EDGE,"E6.sketch_text.stroke-512"),sQuery(id+"F0.wireOp",EDGE,"E6.sketch_text.stroke-513"),sQuery(id+"F0.wireOp",EDGE,"E6.sketch_text.stroke-514"),sQuery(id+"F0.wireOp",EDGE,"E6.sketch_text.stroke-515"),sQuery(id+"F0.wireOp",EDGE,"E6.sketch_text.stroke-523"),sQuery(id+"F0.wireOp",EDGE,"E6.sketch_text.stroke-524"),sQuery(id+"F0.wireOp",EDGE,"E6.sketch_text.stroke-525"),sQuery(id+"F0.wireOp",EDGE,"E6.sketch_text.stroke-526"),sQuery(id+"F0.wireOp",EDGE,"E6.sketch_text.stroke-527"),sQuery(id+"F0.wireOp",EDGE,"E6.sketch_text.stroke-528"),sQuery(id+"F0.wireOp",EDGE,"E6.sketch_text.stroke-529"),sQuery(id+"F0.wireOp",EDGE,"E6.sketch_text.stroke-530"),sQuery(id+"F0.wireOp",EDGE,"E6.sketch_text.stroke-531"),sQuery(id+"F0.wireOp",EDGE,"E6.sketch_text.stroke-532"),sQuery(id+"F0.wireOp",EDGE,"E6.sketch_text.stroke-533"),sQuery(id+"F0.wireOp",EDGE,"E6.sketch_text.stroke-534"),sQuery(id+"F0.wireOp",EDGE,"E6.sketch_text.stroke-535"),sQuery(id+"F0.wireOp",EDGE,"E6.sketch_text.stroke-536"),sQuery(id+"F0.wireOp",EDGE,"E6.sketch_text.stroke-537"),sQuery(id+"F0.wireOp",EDGE,"E6.sketch_text.stroke-538"),sQuery(id+"F0.wireOp",EDGE,"E6.sketch_text.stroke-539"),sQuery(id+"F0.wireOp",EDGE,"E6.sketch_text.stroke-540"),sQuery(id+"F0.wireOp",EDGE,"E6.sketch_text.stroke-541"),sQuery(id+"F0.wireOp",EDGE,"E6.sketch_text.stroke-542"),sQuery(id+"F0.wireOp",EDGE,"E6.sketch_text.stroke-543"),sQuery(id+"F0.wireOp",EDGE,"E6.sketch_text.stroke-544"),sQuery(id+"F0.wireOp",EDGE,"E6.sketch_text.stroke-545"),sQuery(id+"F0.wireOp",EDGE,"E6.sketch_text.stroke-546"),sQuery(id+"F0.wireOp",EDGE,"E6.sketch_text.stroke-547"),sQuery(id+"F0.wireOp",EDGE,"E6.sketch_text.stroke-548"),sQuery(id+"F0.wireOp",EDGE,"E6.sketch_text.stroke-549"),sQuery(id+"F0.wireOp",EDGE,"E6.sketch_text.stroke-550"),sQuery(id+"F0.wireOp",EDGE,"E6.sketch_text.stroke-551"),sQuery(id+"F0.wireOp",EDGE,"E6.sketch_text.stroke-557"),sQuery(id+"F0.wireOp",EDGE,"E6.sketch_text.stroke-558"),sQuery(id+"F0.wireOp",EDGE,"E6.sketch_text.stroke-559"),sQuery(id+"F0.wireOp",EDGE,"E6.sketch_text.stroke-560"),sQuery(id+"F0.wireOp",EDGE,"E6.sketch_text.stroke-561"),sQuery(id+"F0.wireOp",EDGE,"E6.sketch_text.stroke-562"),sQuery(id+"F0.wireOp",EDGE,"E6.sketch_text.stroke-563"),sQuery(id+"F0.wireOp",EDGE,"E6.sketch_text.stroke-564"),sQuery(id+"F0.wireOp",EDGE,"E6.sketch_text.stroke-565"),sQuery(id+"F0.wireOp",EDGE,"E6.sketch_text.stroke-566"),sQuery(id+"F0.wireOp",EDGE,"E6.sketch_text.stroke-567"),sQuery(id+"F0.wireOp",EDGE,"E6.sketch_text.stroke-568"),sQuery(id+"F0.wireOp",EDGE,"E6.sketch_text.stroke-569"),sQuery(id+"F0.wireOp",EDGE,"E6.sketch_text.stroke-570"),sQuery(id+"F0.wireOp",EDGE,"E6.sketch_text.stroke-571"),sQuery(id+"F0.wireOp",EDGE,"E6.sketch_text.stroke-572"),sQuery(id+"F0.wireOp",EDGE,"E6.sketch_text.stroke-573"),sQuery(id+"F0.wireOp",EDGE,"E6.sketch_text.stroke-574"),sQuery(id+"F0.wireOp",EDGE,"E6.sketch_text.stroke-575"),sQuery(id+"F0.wireOp",EDGE,"E6.sketch_text.stroke-576"),sQuery(id+"F0.wireOp",EDGE,"E6.sketch_text.stroke-577"),sQuery(id+"F0.wireOp",EDGE,"E6.sketch_text.stroke-578"),sQuery(id+"F0.wireOp",EDGE,"E6.sketch_text.stroke-589"),sQuery(id+"F0.wireOp",EDGE,"E6.sketch_text.stroke-590"),sQuery(id+"F0.wireOp",EDGE,"E6.sketch_text.stroke-591"),sQuery(id+"F0.wireOp",EDGE,"E6.sketch_text.stroke-592"),sQuery(id+"F0.wireOp",EDGE,"E6.sketch_text.stroke-593"),sQuery(id+"F0.wireOp",EDGE,"E6.sketch_text.stroke-594"),sQuery(id+"F0.wireOp",EDGE,"E6.sketch_text.stroke-595"),sQuery(id+"F0.wireOp",EDGE,"E6.sketch_text.stroke-596"),sQuery(id+"F0.wireOp",EDGE,"E6.sketch_text.stroke-597"),sQuery(id+"F0.wireOp",EDGE,"E6.sketch_text.stroke-598"),sQuery(id+"F0.wireOp",EDGE,"E6.sketch_text.stroke-599"),sQuery(id+"F0.wireOp",EDGE,"E6.sketch_text.stroke-600"),sQuery(id+"F0.wireOp",EDGE,"E6.sketch_text.stroke-601"),sQuery(id+"F0.wireOp",EDGE,"E6.sketch_text.stroke-602"),sQuery(id+"F0.wireOp",EDGE,"E7.sketch_text.stroke-0"),sQuery(id+"F0.wireOp",EDGE,"E7.sketch_text.stroke-1"),sQuery(id+"F0.wireOp",EDGE,"E7.sketch_text.stroke-2"),sQuery(id+"F0.wireOp",EDGE,"E7.sketch_text.stroke-3"),sQuery(id+"F0.wireOp",EDGE,"E7.sketch_text.stroke-4"),sQuery(id+"F0.wireOp",EDGE,"E7.sketch_text.stroke-5"),sQuery(id+"F0.wireOp",EDGE,"E7.sketch_text.stroke-6"),sQuery(id+"F0.wireOp",EDGE,"E7.sketch_text.stroke-7"),sQuery(id+"F0.wireOp",EDGE,"E7.sketch_text.stroke-8"),sQuery(id+"F0.wireOp",EDGE,"E7.sketch_text.stroke-9"),sQuery(id+"F0.wireOp",EDGE,"E7.sketch_text.stroke-10"),sQuery(id+"F0.wireOp",EDGE,"E7.sketch_text.stroke-11"),sQuery(id+"F0.wireOp",EDGE,"E7.sketch_text.stroke-12"),sQuery(id+"F0.wireOp",EDGE,"E7.sketch_text.stroke-13"),sQuery(id+"F0.wireOp",EDGE,"E7.sketch_text.stroke-14"),sQuery(id+"F0.wireOp",EDGE,"E7.sketch_text.stroke-15"),sQuery(id+"F0.wireOp",EDGE,"E7.sketch_text.stroke-16"),sQuery(id+"F0.wireOp",EDGE,"E7.sketch_text.stroke-17"),sQuery(id+"F0.wireOp",EDGE,"E7.sketch_text.stroke-18"),sQuery(id+"F0.wireOp",EDGE,"E7.sketch_text.stroke-19"),sQuery(id+"F0.wireOp",EDGE,"E7.sketch_text.stroke-20"),sQuery(id+"F0.wireOp",EDGE,"E7.sketch_text.stroke-21"),sQuery(id+"F0.wireOp",EDGE,"E7.sketch_text.stroke-22"),sQuery(id+"F0.wireOp",EDGE,"E7.sketch_text.stroke-23"),sQuery(id+"F0.wireOp",EDGE,"E7.sketch_text.stroke-24"),sQuery(id+"F0.wireOp",EDGE,"E7.sketch_text.stroke-25"),sQuery(id+"F0.wireOp",EDGE,"E7.sketch_text.stroke-26"),sQuery(id+"F0.wireOp",EDGE,"E7.sketch_text.stroke-27"),sQuery(id+"F0.wireOp",EDGE,"E7.sketch_text.stroke-28"),sQuery(id+"F0.wireOp",EDGE,"E7.sketch_text.stroke-29"),sQuery(id+"F0.wireOp",EDGE,"E7.sketch_text.stroke-30"),sQuery(id+"F0.wireOp",EDGE,"E7.sketch_text.stroke-45"),sQuery(id+"F0.wireOp",EDGE,"E7.sketch_text.stroke-46"),sQuery(id+"F0.wireOp",EDGE,"E7.sketch_text.stroke-47"),sQuery(id+"F0.wireOp",EDGE,"E7.sketch_text.stroke-48"),sQuery(id+"F0.wireOp",EDGE,"E7.sketch_text.stroke-49"),sQuery(id+"F0.wireOp",EDGE,"E7.sketch_text.stroke-50"),sQuery(id+"F0.wireOp",EDGE,"E7.sketch_text.stroke-51"),sQuery(id+"F0.wireOp",EDGE,"E7.sketch_text.stroke-52"),sQuery(id+"F0.wireOp",EDGE,"E7.sketch_text.stroke-53"),sQuery(id+"F0.wireOp",EDGE,"E7.sketch_text.stroke-54"),sQuery(id+"F0.wireOp",EDGE,"E7.sketch_text.stroke-55"),sQuery(id+"F0.wireOp",EDGE,"E7.sketch_text.stroke-63"),sQuery(id+"F0.wireOp",EDGE,"E7.sketch_text.stroke-64"),sQuery(id+"F0.wireOp",EDGE,"E7.sketch_text.stroke-65"),sQuery(id+"F0.wireOp",EDGE,"E7.sketch_text.stroke-66"),sQuery(id+"F0.wireOp",EDGE,"E7.sketch_text.stroke-67"),sQuery(id+"F0.wireOp",EDGE,"E7.sketch_text.stroke-68"),sQuery(id+"F0.wireOp",EDGE,"E7.sketch_text.stroke-69"),sQuery(id+"F0.wireOp",EDGE,"E7.sketch_text.stroke-70"),sQuery(id+"F0.wireOp",EDGE,"E7.sketch_text.stroke-71"),sQuery(id+"F0.wireOp",EDGE,"E7.sketch_text.stroke-72"),sQuery(id+"F0.wireOp",EDGE,"E7.sketch_text.stroke-73"),sQuery(id+"F0.wireOp",EDGE,"E7.sketch_text.stroke-74"),sQuery(id+"F0.wireOp",EDGE,"E7.sketch_text.stroke-75"),sQuery(id+"F0.wireOp",EDGE,"E7.sketch_text.stroke-76"),sQuery(id+"F0.wireOp",EDGE,"E7.sketch_text.stroke-77"),sQuery(id+"F0.wireOp",EDGE,"E7.sketch_text.stroke-78"),sQuery(id+"F0.wireOp",EDGE,"E7.sketch_text.stroke-79"),sQuery(id+"F0.wireOp",EDGE,"E7.sketch_text.stroke-80"),sQuery(id+"F0.wireOp",EDGE,"E7.sketch_text.stroke-81"),sQuery(id+"F0.wireOp",EDGE,"E7.sketch_text.stroke-82"),sQuery(id+"F0.wireOp",EDGE,"E7.sketch_text.stroke-83"),sQuery(id+"F0.wireOp",EDGE,"E7.sketch_text.stroke-84"),sQuery(id+"F0.wireOp",EDGE,"E7.sketch_text.stroke-85"),sQuery(id+"F0.wireOp",EDGE,"E7.sketch_text.stroke-86"),sQuery(id+"F0.wireOp",EDGE,"E7.sketch_text.stroke-87"),sQuery(id+"F0.wireOp",EDGE,"E7.sketch_text.stroke-88"),sQuery(id+"F0.wireOp",EDGE,"E7.sketch_text.stroke-89"),sQuery(id+"F0.wireOp",EDGE,"E7.sketch_text.stroke-90"),sQuery(id+"F0.wireOp",EDGE,"E7.sketch_text.stroke-91"),sQuery(id+"F0.wireOp",EDGE,"E7.sketch_text.stroke-92"),sQuery(id+"F0.wireOp",EDGE,"E7.sketch_text.stroke-93"),sQuery(id+"F0.wireOp",EDGE,"E7.sketch_text.stroke-94"),sQuery(id+"F0.wireOp",EDGE,"E7.sketch_text.stroke-95"),sQuery(id+"F0.wireOp",EDGE,"E7.sketch_text.stroke-96"),sQuery(id+"F0.wireOp",EDGE,"E7.sketch_text.stroke-97"),sQuery(id+"F0.wireOp",EDGE,"E7.sketch_text.stroke-98"),sQuery(id+"F0.wireOp",EDGE,"E7.sketch_text.stroke-99"),sQuery(id+"F0.wireOp",EDGE,"E7.sketch_text.stroke-100"),sQuery(id+"F0.wireOp",EDGE,"E7.sketch_text.stroke-101"),sQuery(id+"F0.wireOp",EDGE,"E7.sketch_text.stroke-102"),sQuery(id+"F0.wireOp",EDGE,"E7.sketch_text.stroke-103"),sQuery(id+"F0.wireOp",EDGE,"E7.sketch_text.stroke-109"),sQuery(id+"F0.wireOp",EDGE,"E7.sketch_text.stroke-110"),sQuery(id+"F0.wireOp",EDGE,"E7.sketch_text.stroke-111"),sQuery(id+"F0.wireOp",EDGE,"E7.sketch_text.stroke-112"),sQuery(id+"F0.wireOp",EDGE,"E7.sketch_text.stroke-113"),sQuery(id+"F0.wireOp",EDGE,"E7.sketch_text.stroke-114"),sQuery(id+"F0.wireOp",EDGE,"E7.sketch_text.stroke-115"),sQuery(id+"F0.wireOp",EDGE,"E7.sketch_text.stroke-116"),sQuery(id+"F0.wireOp",EDGE,"E7.sketch_text.stroke-117"),sQuery(id+"F0.wireOp",EDGE,"E7.sketch_text.stroke-118"),sQuery(id+"F0.wireOp",EDGE,"E7.sketch_text.stroke-119"),sQuery(id+"F0.wireOp",EDGE,"E7.sketch_text.stroke-120"),sQuery(id+"F0.wireOp",EDGE,"E7.sketch_text.stroke-121"),sQuery(id+"F0.wireOp",EDGE,"E7.sketch_text.stroke-122"),sQuery(id+"F0.wireOp",EDGE,"E7.sketch_text.stroke-123"),sQuery(id+"F0.wireOp",EDGE,"E7.sketch_text.stroke-124"),sQuery(id+"F0.wireOp",EDGE,"E7.sketch_text.stroke-125"),sQuery(id+"F0.wireOp",EDGE,"E7.sketch_text.stroke-126"),sQuery(id+"F0.wireOp",EDGE,"E7.sketch_text.stroke-127"),sQuery(id+"F0.wireOp",EDGE,"E7.sketch_text.stroke-128"),sQuery(id+"F0.wireOp",EDGE,"E7.sketch_text.stroke-129"),sQuery(id+"F0.wireOp",EDGE,"E7.sketch_text.stroke-130"),sQuery(id+"F0.wireOp",EDGE,"E7.sketch_text.stroke-139"),sQuery(id+"F0.wireOp",EDGE,"E7.sketch_text.stroke-140"),sQuery(id+"F0.wireOp",EDGE,"E7.sketch_text.stroke-141"),sQuery(id+"F0.wireOp",EDGE,"E7.sketch_text.stroke-142"),sQuery(id+"F0.wireOp",EDGE,"E7.sketch_text.stroke-143"),sQuery(id+"F0.wireOp",EDGE,"E7.sketch_text.stroke-144"),sQuery(id+"F0.wireOp",EDGE,"E7.sketch_text.stroke-145"),sQuery(id+"F0.wireOp",EDGE,"E7.sketch_text.stroke-146"),sQuery(id+"F0.wireOp",EDGE,"E7.sketch_text.stroke-147"),sQuery(id+"F0.wireOp",EDGE,"E7.sketch_text.stroke-148"),sQuery(id+"F0.wireOp",EDGE,"E7.sketch_text.stroke-149"),sQuery(id+"F0.wireOp",EDGE,"E7.sketch_text.stroke-150"),sQuery(id+"F0.wireOp",EDGE,"E7.sketch_text.stroke-151"),sQuery(id+"F0.wireOp",EDGE,"E7.sketch_text.stroke-152"),sQuery(id+"F0.wireOp",EDGE,"E7.sketch_text.stroke-153"),sQuery(id+"F0.wireOp",EDGE,"E7.sketch_text.stroke-154"),sQuery(id+"F0.wireOp",EDGE,"E7.sketch_text.stroke-155"),sQuery(id+"F0.wireOp",EDGE,"E7.sketch_text.stroke-156"),sQuery(id+"F0.wireOp",EDGE,"E7.sketch_text.stroke-157"),sQuery(id+"F0.wireOp",EDGE,"E7.sketch_text.stroke-158"),sQuery(id+"F0.wireOp",EDGE,"E7.sketch_text.stroke-159"),sQuery(id+"F0.wireOp",EDGE,"E7.sketch_text.stroke-160"),sQuery(id+"F0.wireOp",EDGE,"E7.sketch_text.stroke-161"),sQuery(id+"F0.wireOp",EDGE,"E7.sketch_text.stroke-162"),sQuery(id+"F0.wireOp",EDGE,"E7.sketch_text.stroke-163"),sQuery(id+"F0.wireOp",EDGE,"E7.sketch_text.stroke-164"),sQuery(id+"F0.wireOp",EDGE,"E7.sketch_text.stroke-165"),sQuery(id+"F0.wireOp",EDGE,"E7.sketch_text.stroke-166"),sQuery(id+"F0.wireOp",EDGE,"E7.sketch_text.stroke-167"),sQuery(id+"F0.wireOp",EDGE,"E7.sketch_text.stroke-168"),sQuery(id+"F0.wireOp",EDGE,"E7.sketch_text.stroke-169"),sQuery(id+"F0.wireOp",EDGE,"E7.sketch_text.stroke-170"),sQuery(id+"F0.wireOp",EDGE,"E7.sketch_text.stroke-171"),sQuery(id+"F0.wireOp",EDGE,"E7.sketch_text.stroke-172"),sQuery(id+"F0.wireOp",EDGE,"E7.sketch_text.stroke-173"),sQuery(id+"F0.wireOp",EDGE,"E7.sketch_text.stroke-174"),sQuery(id+"F0.wireOp",EDGE,"E7.sketch_text.stroke-175"),sQuery(id+"F0.wireOp",EDGE,"E7.sketch_text.stroke-176"),sQuery(id+"F0.wireOp",EDGE,"E7.sketch_text.stroke-177"),sQuery(id+"F0.wireOp",EDGE,"E7.sketch_text.stroke-178"),sQuery(id+"F0.wireOp",EDGE,"E7.sketch_text.stroke-179"),sQuery(id+"F0.wireOp",EDGE,"E7.sketch_text.stroke-180"),sQuery(id+"F0.wireOp",EDGE,"E7.sketch_text.stroke-181"),sQuery(id+"F0.wireOp",EDGE,"E7.sketch_text.stroke-182"),sQuery(id+"F0.wireOp",EDGE,"E7.sketch_text.stroke-183"),sQuery(id+"F0.wireOp",EDGE,"E7.sketch_text.stroke-184"),sQuery(id+"F0.wireOp",EDGE,"E7.sketch_text.stroke-185"),sQuery(id+"F0.wireOp",EDGE,"E7.sketch_text.stroke-186"),sQuery(id+"F0.wireOp",EDGE,"E7.sketch_text.stroke-187"),sQuery(id+"F0.wireOp",EDGE,"E7.sketch_text.stroke-188"),sQuery(id+"F0.wireOp",EDGE,"E7.sketch_text.stroke-189"),sQuery(id+"F0.wireOp",EDGE,"E7.sketch_text.stroke-190"),sQuery(id+"F0.wireOp",EDGE,"E7.sketch_text.stroke-191"),sQuery(id+"F0.wireOp",EDGE,"E7.sketch_text.stroke-197"),sQuery(id+"F0.wireOp",EDGE,"E7.sketch_text.stroke-198"),sQuery(id+"F0.wireOp",EDGE,"E7.sketch_text.stroke-199"),sQuery(id+"F0.wireOp",EDGE,"E7.sketch_text.stroke-200"),sQuery(id+"F0.wireOp",EDGE,"E7.sketch_text.stroke-201"),sQuery(id+"F0.wireOp",EDGE,"E7.sketch_text.stroke-202"),sQuery(id+"F0.wireOp",EDGE,"E7.sketch_text.stroke-203"),sQuery(id+"F0.wireOp",EDGE,"E7.sketch_text.stroke-204"),sQuery(id+"F0.wireOp",EDGE,"E7.sketch_text.stroke-205"),sQuery(id+"F0.wireOp",EDGE,"E7.sketch_text.stroke-206"),sQuery(id+"F0.wireOp",EDGE,"E7.sketch_text.stroke-207"),sQuery(id+"F0.wireOp",EDGE,"E7.sketch_text.stroke-208"),sQuery(id+"F0.wireOp",EDGE,"E7.sketch_text.stroke-209"),sQuery(id+"F0.wireOp",EDGE,"E7.sketch_text.stroke-210"),sQuery(id+"F0.wireOp",EDGE,"E7.sketch_text.stroke-211"),sQuery(id+"F0.wireOp",EDGE,"E7.sketch_text.stroke-212"),sQuery(id+"F0.wireOp",EDGE,"E7.sketch_text.stroke-213"),sQuery(id+"F0.wireOp",EDGE,"E7.sketch_text.stroke-214"),sQuery(id+"F0.wireOp",EDGE,"E7.sketch_text.stroke-215"),sQuery(id+"F0.wireOp",EDGE,"E7.sketch_text.stroke-216"),sQuery(id+"F0.wireOp",EDGE,"E7.sketch_text.stroke-217"),sQuery(id+"F0.wireOp",EDGE,"E7.sketch_text.stroke-218"),sQuery(id+"F0.wireOp",EDGE,"E7.sketch_text.stroke-219"),sQuery(id+"F0.wireOp",EDGE,"E7.sketch_text.stroke-220"),sQuery(id+"F0.wireOp",EDGE,"E7.sketch_text.stroke-221"),sQuery(id+"F0.wireOp",EDGE,"E7.sketch_text.stroke-222"),sQuery(id+"F0.wireOp",EDGE,"E7.sketch_text.stroke-223"),sQuery(id+"F0.wireOp",EDGE,"E7.sketch_text.stroke-224"),sQuery(id+"F0.wireOp",EDGE,"E7.sketch_text.stroke-225"),sQuery(id+"F0.wireOp",EDGE,"E7.sketch_text.stroke-226"),sQuery(id+"F0.wireOp",EDGE,"E7.sketch_text.stroke-227"),sQuery(id+"F0.wireOp",EDGE,"E7.sketch_text.stroke-228"),sQuery(id+"F0.wireOp",EDGE,"E7.sketch_text.stroke-229"),sQuery(id+"F0.wireOp",EDGE,"E7.sketch_text.stroke-230"),sQuery(id+"F0.wireOp",EDGE,"E7.sketch_text.stroke-231"),sQuery(id+"F0.wireOp",EDGE,"E7.sketch_text.stroke-232"),sQuery(id+"F0.wireOp",EDGE,"E7.sketch_text.stroke-233"),sQuery(id+"F0.wireOp",EDGE,"E7.sketch_text.stroke-234"),sQuery(id+"F0.wireOp",EDGE,"E7.sketch_text.stroke-235"),sQuery(id+"F0.wireOp",EDGE,"E7.sketch_text.stroke-236"),sQuery(id+"F0.wireOp",EDGE,"E7.sketch_text.stroke-237"),sQuery(id+"F0.wireOp",EDGE,"E7.sketch_text.stroke-238"),sQuery(id+"F0.wireOp",EDGE,"E7.sketch_text.stroke-239"),sQuery(id+"F0.wireOp",EDGE,"E7.sketch_text.stroke-240"),sQuery(id+"F0.wireOp",EDGE,"E7.sketch_text.stroke-241"),sQuery(id+"F0.wireOp",EDGE,"E7.sketch_text.stroke-242"),sQuery(id+"F0.wireOp",EDGE,"E7.sketch_text.stroke-243"),sQuery(id+"F0.wireOp",EDGE,"E7.sketch_text.stroke-244"),sQuery(id+"F0.wireOp",EDGE,"E7.sketch_text.stroke-245"),sQuery(id+"F0.wireOp",EDGE,"E7.sketch_text.stroke-246"),sQuery(id+"F0.wireOp",EDGE,"E7.sketch_text.stroke-247"),sQuery(id+"F0.wireOp",EDGE,"E7.sketch_text.stroke-248"),sQuery(id+"F0.wireOp",EDGE,"E7.sketch_text.stroke-249"),sQuery(id+"F0.wireOp",EDGE,"E7.sketch_text.stroke-250"),sQuery(id+"F0.wireOp",EDGE,"E7.sketch_text.stroke-251"),sQuery(id+"F0.wireOp",EDGE,"E7.sketch_text.stroke-252"),sQuery(id+"F0.wireOp",EDGE,"E7.sketch_text.stroke-253"),sQuery(id+"F0.wireOp",EDGE,"E7.sketch_text.stroke-254"),sQuery(id+"F0.wireOp",EDGE,"E7.sketch_text.stroke-255"),sQuery(id+"F0.wireOp",EDGE,"E7.sketch_text.stroke-256"),sQuery(id+"F0.wireOp",EDGE,"E7.sketch_text.stroke-257"),sQuery(id+"F0.wireOp",EDGE,"E7.sketch_text.stroke-258"),sQuery(id+"F0.wireOp",EDGE,"E7.sketch_text.stroke-259"),sQuery(id+"F0.wireOp",EDGE,"E7.sketch_text.stroke-260"),sQuery(id+"F0.wireOp",EDGE,"E7.sketch_text.stroke-261"),sQuery(id+"F0.wireOp",EDGE,"E7.sketch_text.stroke-262"),sQuery(id+"F0.wireOp",EDGE,"E7.sketch_text.stroke-263"),sQuery(id+"F0.wireOp",EDGE,"E7.sketch_text.stroke-264"),sQuery(id+"F0.wireOp",EDGE,"E7.sketch_text.stroke-265"),sQuery(id+"F0.wireOp",EDGE,"E7.sketch_text.stroke-271"),sQuery(id+"F0.wireOp",EDGE,"E7.sketch_text.stroke-272"),sQuery(id+"F0.wireOp",EDGE,"E7.sketch_text.stroke-273"),sQuery(id+"F0.wireOp",EDGE,"E7.sketch_text.stroke-274"),sQuery(id+"F0.wireOp",EDGE,"E7.sketch_text.stroke-275"),sQuery(id+"F0.wireOp",EDGE,"E7.sketch_text.stroke-276"),sQuery(id+"F0.wireOp",EDGE,"E7.sketch_text.stroke-277"),sQuery(id+"F0.wireOp",EDGE,"E7.sketch_text.stroke-278"),sQuery(id+"F0.wireOp",EDGE,"E7.sketch_text.stroke-279"),sQuery(id+"F0.wireOp",EDGE,"E7.sketch_text.stroke-280"),sQuery(id+"F0.wireOp",EDGE,"E7.sketch_text.stroke-281"),sQuery(id+"F0.wireOp",EDGE,"E7.sketch_text.stroke-282"),sQuery(id+"F0.wireOp",EDGE,"E7.sketch_text.stroke-283"),sQuery(id+"F0.wireOp",EDGE,"E7.sketch_text.stroke-284"),sQuery(id+"F0.wireOp",EDGE,"E7.sketch_text.stroke-285"),sQuery(id+"F0.wireOp",EDGE,"E7.sketch_text.stroke-286"),sQuery(id+"F0.wireOp",EDGE,"E7.sketch_text.stroke-287"),sQuery(id+"F0.wireOp",EDGE,"E7.sketch_text.stroke-288"),sQuery(id+"F0.wireOp",EDGE,"E7.sketch_text.stroke-289"),sQuery(id+"F0.wireOp",EDGE,"E7.sketch_text.stroke-290"),sQuery(id+"F0.wireOp",EDGE,"E7.sketch_text.stroke-291"),sQuery(id+"F0.wireOp",EDGE,"E7.sketch_text.stroke-292"),sQuery(id+"F0.wireOp",EDGE,"E7.sketch_text.stroke-293"),sQuery(id+"F0.wireOp",EDGE,"E7.sketch_text.stroke-294"),sQuery(id+"F0.wireOp",EDGE,"E7.sketch_text.stroke-295"),sQuery(id+"F0.wireOp",EDGE,"E7.sketch_text.stroke-296"),sQuery(id+"F0.wireOp",EDGE,"E7.sketch_text.stroke-297"),sQuery(id+"F0.wireOp",EDGE,"E7.sketch_text.stroke-298"),sQuery(id+"F0.wireOp",EDGE,"E7.sketch_text.stroke-299"),sQuery(id+"F0.wireOp",EDGE,"E7.sketch_text.stroke-300"),sQuery(id+"F0.wireOp",EDGE,"E7.sketch_text.stroke-306"),sQuery(id+"F0.wireOp",EDGE,"E7.sketch_text.stroke-307"),sQuery(id+"F0.wireOp",EDGE,"E7.sketch_text.stroke-308"),sQuery(id+"F0.wireOp",EDGE,"E7.sketch_text.stroke-309"),sQuery(id+"F0.wireOp",EDGE,"E7.sketch_text.stroke-310"),sQuery(id+"F0.wireOp",EDGE,"E7.sketch_text.stroke-311"),sQuery(id+"F0.wireOp",EDGE,"E7.sketch_text.stroke-312"),sQuery(id+"F0.wireOp",EDGE,"E7.sketch_text.stroke-313"),sQuery(id+"F0.wireOp",EDGE,"E7.sketch_text.stroke-314"),sQuery(id+"F0.wireOp",EDGE,"E7.sketch_text.stroke-315"),sQuery(id+"F0.wireOp",EDGE,"E7.sketch_text.stroke-316"),sQuery(id+"F0.wireOp",EDGE,"E7.sketch_text.stroke-317"),sQuery(id+"F0.wireOp",EDGE,"E7.sketch_text.stroke-318"),sQuery(id+"F0.wireOp",EDGE,"E7.sketch_text.stroke-319"),sQuery(id+"F0.wireOp",EDGE,"E7.sketch_text.stroke-320"),sQuery(id+"F0.wireOp",EDGE,"E7.sketch_text.stroke-321"),sQuery(id+"F0.wireOp",EDGE,"E7.sketch_text.stroke-322"),sQuery(id+"F0.wireOp",EDGE,"E7.sketch_text.stroke-323"),sQuery(id+"F0.wireOp",EDGE,"E7.sketch_text.stroke-324"),sQuery(id+"F0.wireOp",EDGE,"E7.sketch_text.stroke-325"),sQuery(id+"F0.wireOp",EDGE,"E7.sketch_text.stroke-326"),sQuery(id+"F0.wireOp",EDGE,"E7.sketch_text.stroke-327"),sQuery(id+"F0.wireOp",EDGE,"E7.sketch_text.stroke-328"),sQuery(id+"F0.wireOp",EDGE,"E7.sketch_text.stroke-329"),sQuery(id+"F0.wireOp",EDGE,"E7.sketch_text.stroke-330"),sQuery(id+"F0.wireOp",EDGE,"E7.sketch_text.stroke-331"),sQuery(id+"F0.wireOp",EDGE,"E7.sketch_text.stroke-332"),sQuery(id+"F0.wireOp",EDGE,"E7.sketch_text.stroke-333"),sQuery(id+"F0.wireOp",EDGE,"E7.sketch_text.stroke-334"),sQuery(id+"F0.wireOp",EDGE,"E7.sketch_text.stroke-335"),sQuery(id+"F0.wireOp",EDGE,"E7.sketch_text.stroke-336"),sQuery(id+"F0.wireOp",EDGE,"E7.sketch_text.stroke-337"),sQuery(id+"F0.wireOp",EDGE,"E7.sketch_text.stroke-338"),sQuery(id+"F0.wireOp",EDGE,"E7.sketch_text.stroke-339"),sQuery(id+"F0.wireOp",EDGE,"E7.sketch_text.stroke-340"),sQuery(id+"F0.wireOp",EDGE,"E7.sketch_text.stroke-341"),sQuery(id+"F0.wireOp",EDGE,"E7.sketch_text.stroke-342"),sQuery(id+"F0.wireOp",EDGE,"E7.sketch_text.stroke-343"),sQuery(id+"F0.wireOp",EDGE,"E7.sketch_text.stroke-344"),sQuery(id+"F0.wireOp",EDGE,"E7.sketch_text.stroke-345"),sQuery(id+"F0.wireOp",EDGE,"E7.sketch_text.stroke-346"),sQuery(id+"F0.wireOp",EDGE,"E7.sketch_text.stroke-347"),sQuery(id+"F0.wireOp",EDGE,"E7.sketch_text.stroke-348"),sQuery(id+"F0.wireOp",EDGE,"E7.sketch_text.stroke-349"),sQuery(id+"F0.wireOp",EDGE,"E7.sketch_text.stroke-350"),sQuery(id+"F0.wireOp",EDGE,"E7.sketch_text.stroke-351"),sQuery(id+"F0.wireOp",EDGE,"E7.sketch_text.stroke-352"),sQuery(id+"F0.wireOp",EDGE,"E7.sketch_text.stroke-353"),sQuery(id+"F0.wireOp",EDGE,"E7.sketch_text.stroke-354"),sQuery(id+"F0.wireOp",EDGE,"E7.sketch_text.stroke-355"),sQuery(id+"F0.wireOp",EDGE,"E7.sketch_text.stroke-356"),sQuery(id+"F0.wireOp",EDGE,"E7.sketch_text.stroke-357"),sQuery(id+"F0.wireOp",EDGE,"E7.sketch_text.stroke-358"),sQuery(id+"F0.wireOp",EDGE,"E7.sketch_text.stroke-359"),sQuery(id+"F0.wireOp",EDGE,"E7.sketch_text.stroke-360"),sQuery(id+"F0.wireOp",EDGE,"E7.sketch_text.stroke-361"),sQuery(id+"F0.wireOp",EDGE,"E7.sketch_text.stroke-362"),sQuery(id+"F0.wireOp",EDGE,"E7.sketch_text.stroke-363"),sQuery(id+"F0.wireOp",EDGE,"E7.sketch_text.stroke-364"),sQuery(id+"F0.wireOp",EDGE,"E7.sketch_text.stroke-365"),sQuery(id+"F0.wireOp",EDGE,"E7.sketch_text.stroke-366"),sQuery(id+"F0.wireOp",EDGE,"E7.sketch_text.stroke-367"),sQuery(id+"F0.wireOp",EDGE,"E7.sketch_text.stroke-368"),sQuery(id+"F0.wireOp",EDGE,"E7.sketch_text.stroke-369"),sQuery(id+"F0.wireOp",EDGE,"E7.sketch_text.stroke-370"),sQuery(id+"F0.wireOp",EDGE,"E7.sketch_text.stroke-371"),sQuery(id+"F0.wireOp",EDGE,"E7.sketch_text.stroke-372"),sQuery(id+"F0.wireOp",EDGE,"E7.sketch_text.stroke-373"),sQuery(id+"F0.wireOp",EDGE,"E7.sketch_text.stroke-374"),sQuery(id+"F0.wireOp",EDGE,"E7.sketch_text.stroke-375"),sQuery(id+"F0.wireOp",EDGE,"E7.sketch_text.stroke-376"),sQuery(id+"F0.wireOp",EDGE,"E7.sketch_text.stroke-377"),sQuery(id+"F0.wireOp",EDGE,"E7.sketch_text.stroke-378"),sQuery(id+"F0.wireOp",EDGE,"E7.sketch_text.stroke-379"),sQuery(id+"F0.wireOp",EDGE,"E7.sketch_text.stroke-380"),sQuery(id+"F0.wireOp",EDGE,"E7.sketch_text.stroke-381"),sQuery(id+"F0.wireOp",EDGE,"E7.sketch_text.stroke-382"),sQuery(id+"F0.wireOp",EDGE,"E7.sketch_text.stroke-383"),sQuery(id+"F0.wireOp",EDGE,"E7.sketch_text.stroke-384"),sQuery(id+"F0.wireOp",EDGE,"E7.sketch_text.stroke-385"),sQuery(id+"F0.wireOp",EDGE,"E7.sketch_text.stroke-386"),sQuery(id+"F0.wireOp",EDGE,"E7.sketch_text.stroke-387"),sQuery(id+"F0.wireOp",EDGE,"E7.sketch_text.stroke-388"),sQuery(id+"F0.wireOp",EDGE,"E7.sketch_text.stroke-389"),sQuery(id+"F0.wireOp",EDGE,"E7.sketch_text.stroke-390"),sQuery(id+"F0.wireOp",EDGE,"E7.sketch_text.stroke-391"),sQuery(id+"F0.wireOp",EDGE,"E7.sketch_text.stroke-392"),sQuery(id+"F0.wireOp",EDGE,"E7.sketch_text.stroke-393"),sQuery(id+"F0.wireOp",EDGE,"E7.sketch_text.stroke-394"),sQuery(id+"F0.wireOp",EDGE,"E7.sketch_text.stroke-409"),sQuery(id+"F0.wireOp",EDGE,"E7.sketch_text.stroke-410"),sQuery(id+"F0.wireOp",EDGE,"E7.sketch_text.stroke-411"),sQuery(id+"F0.wireOp",EDGE,"E7.sketch_text.stroke-412"),sQuery(id+"F0.wireOp",EDGE,"E7.sketch_text.stroke-413"),sQuery(id+"F0.wireOp",EDGE,"E7.sketch_text.stroke-414"),sQuery(id+"F0.wireOp",EDGE,"E7.sketch_text.stroke-415"),sQuery(id+"F0.wireOp",EDGE,"E7.sketch_text.stroke-416"),sQuery(id+"F0.wireOp",EDGE,"E7.sketch_text.stroke-417"),sQuery(id+"F0.wireOp",EDGE,"E7.sketch_text.stroke-418"),sQuery(id+"F0.wireOp",EDGE,"E7.sketch_text.stroke-419"),sQuery(id+"F0.wireOp",EDGE,"E7.sketch_text.stroke-427"),sQuery(id+"F0.wireOp",EDGE,"E7.sketch_text.stroke-428"),sQuery(id+"F0.wireOp",EDGE,"E7.sketch_text.stroke-429"),sQuery(id+"F0.wireOp",EDGE,"E7.sketch_text.stroke-430"),sQuery(id+"F0.wireOp",EDGE,"E7.sketch_text.stroke-431"),sQuery(id+"F0.wireOp",EDGE,"E7.sketch_text.stroke-432"),sQuery(id+"F0.wireOp",EDGE,"E7.sketch_text.stroke-433"),sQuery(id+"F0.wireOp",EDGE,"E7.sketch_text.stroke-434"),sQuery(id+"F0.wireOp",EDGE,"E7.sketch_text.stroke-435"),sQuery(id+"F0.wireOp",EDGE,"E7.sketch_text.stroke-436"),sQuery(id+"F0.wireOp",EDGE,"E7.sketch_text.stroke-437"),sQuery(id+"F0.wireOp",EDGE,"E7.sketch_text.stroke-438"),sQuery(id+"F0.wireOp",EDGE,"E7.sketch_text.stroke-439"),sQuery(id+"F0.wireOp",EDGE,"E7.sketch_text.stroke-440"),sQuery(id+"F0.wireOp",EDGE,"E7.sketch_text.stroke-441"),sQuery(id+"F0.wireOp",EDGE,"E7.sketch_text.stroke-442"),sQuery(id+"F0.wireOp",EDGE,"E7.sketch_text.stroke-443"),sQuery(id+"F0.wireOp",EDGE,"E7.sketch_text.stroke-444"),sQuery(id+"F0.wireOp",EDGE,"E7.sketch_text.stroke-445"),sQuery(id+"F0.wireOp",EDGE,"E7.sketch_text.stroke-446"),sQuery(id+"F0.wireOp",EDGE,"E7.sketch_text.stroke-447"),sQuery(id+"F0.wireOp",EDGE,"E7.sketch_text.stroke-448"),sQuery(id+"F0.wireOp",EDGE,"E7.sketch_text.stroke-449"),sQuery(id+"F0.wireOp",EDGE,"E7.sketch_text.stroke-450"),sQuery(id+"F0.wireOp",EDGE,"E7.sketch_text.stroke-451"),sQuery(id+"F0.wireOp",EDGE,"E7.sketch_text.stroke-452"),sQuery(id+"F0.wireOp",EDGE,"E7.sketch_text.stroke-453"),sQuery(id+"F0.wireOp",EDGE,"E7.sketch_text.stroke-459"),sQuery(id+"F0.wireOp",EDGE,"E7.sketch_text.stroke-460"),sQuery(id+"F0.wireOp",EDGE,"E7.sketch_text.stroke-461"),sQuery(id+"F0.wireOp",EDGE,"E7.sketch_text.stroke-462"),sQuery(id+"F0.wireOp",EDGE,"E7.sketch_text.stroke-463"),sQuery(id+"F0.wireOp",EDGE,"E7.sketch_text.stroke-464"),sQuery(id+"F0.wireOp",EDGE,"E7.sketch_text.stroke-465"),sQuery(id+"F0.wireOp",EDGE,"E7.sketch_text.stroke-466"),sQuery(id+"F0.wireOp",EDGE,"E7.sketch_text.stroke-467"),sQuery(id+"F0.wireOp",EDGE,"E7.sketch_text.stroke-468"),sQuery(id+"F0.wireOp",EDGE,"E7.sketch_text.stroke-469"),sQuery(id+"F0.wireOp",EDGE,"E7.sketch_text.stroke-470"),sQuery(id+"F0.wireOp",EDGE,"E7.sketch_text.stroke-471"),sQuery(id+"F0.wireOp",EDGE,"E7.sketch_text.stroke-472"),sQuery(id+"F0.wireOp",EDGE,"E7.sketch_text.stroke-473"),sQuery(id+"F0.wireOp",EDGE,"E7.sketch_text.stroke-474"),sQuery(id+"F0.wireOp",EDGE,"E7.sketch_text.stroke-475"),sQuery(id+"F0.wireOp",EDGE,"E7.sketch_text.stroke-476"),sQuery(id+"F0.wireOp",EDGE,"E7.sketch_text.stroke-477"),sQuery(id+"F0.wireOp",EDGE,"E7.sketch_text.stroke-478"),sQuery(id+"F0.wireOp",EDGE,"E7.sketch_text.stroke-487"),sQuery(id+"F0.wireOp",EDGE,"E7.sketch_text.stroke-488"),sQuery(id+"F0.wireOp",EDGE,"E7.sketch_text.stroke-489"),sQuery(id+"F0.wireOp",EDGE,"E7.sketch_text.stroke-490"),sQuery(id+"F0.wireOp",EDGE,"E7.sketch_text.stroke-491"),sQuery(id+"F0.wireOp",EDGE,"E7.sketch_text.stroke-492"),sQuery(id+"F0.wireOp",EDGE,"E7.sketch_text.stroke-493"),sQuery(id+"F0.wireOp",EDGE,"E7.sketch_text.stroke-494"),sQuery(id+"F0.wireOp",EDGE,"E7.sketch_text.stroke-495"),sQuery(id+"F0.wireOp",EDGE,"E7.sketch_text.stroke-496"),sQuery(id+"F0.wireOp",EDGE,"E7.sketch_text.stroke-497"),sQuery(id+"F0.wireOp",EDGE,"E7.sketch_text.stroke-498"),sQuery(id+"F0.wireOp",EDGE,"E7.sketch_text.stroke-499"),sQuery(id+"F0.wireOp",EDGE,"E7.sketch_text.stroke-500"),sQuery(id+"F0.wireOp",EDGE,"E7.sketch_text.stroke-501")])],"isStart":false});
            var sketch = newSketch(context, id + "F2", { "sketchPlane" : qUnion([Q0])});
            skLineSegment(sketch, "E8", {"start": v(-66, 0) * mm, "end": v(66, 0) * mm});
            skLineSegment(sketch, "E9", {"start": v(-66, 0) * mm, "end": v(-66, 0) * mm});
            skLineSegment(sketch, "E10", {"start": v(66, 0) * mm, "end": v(66, 0) * mm});
            skSolve(sketch);
        }
        {
            var Q0;
            Q0=makeQuery(id+"F2.imprint","IMPRINT",FACE,{"disambiguationData":[TD([[makeQuery(id+"F2.imprint","IMPRINT",EDGE,{"derivedFrom":sQuery(id+"F2.wireOp",EDGE,"E8")}),-1.0]])]});
            extrude(context, id + "F3", {"entities" : qUnion([Q0]), "operationType" : NewBodyOperationType.ADD, "depth" : 0.01 * mm, "offsetDistance" : 25 * mm});
        }
    });
